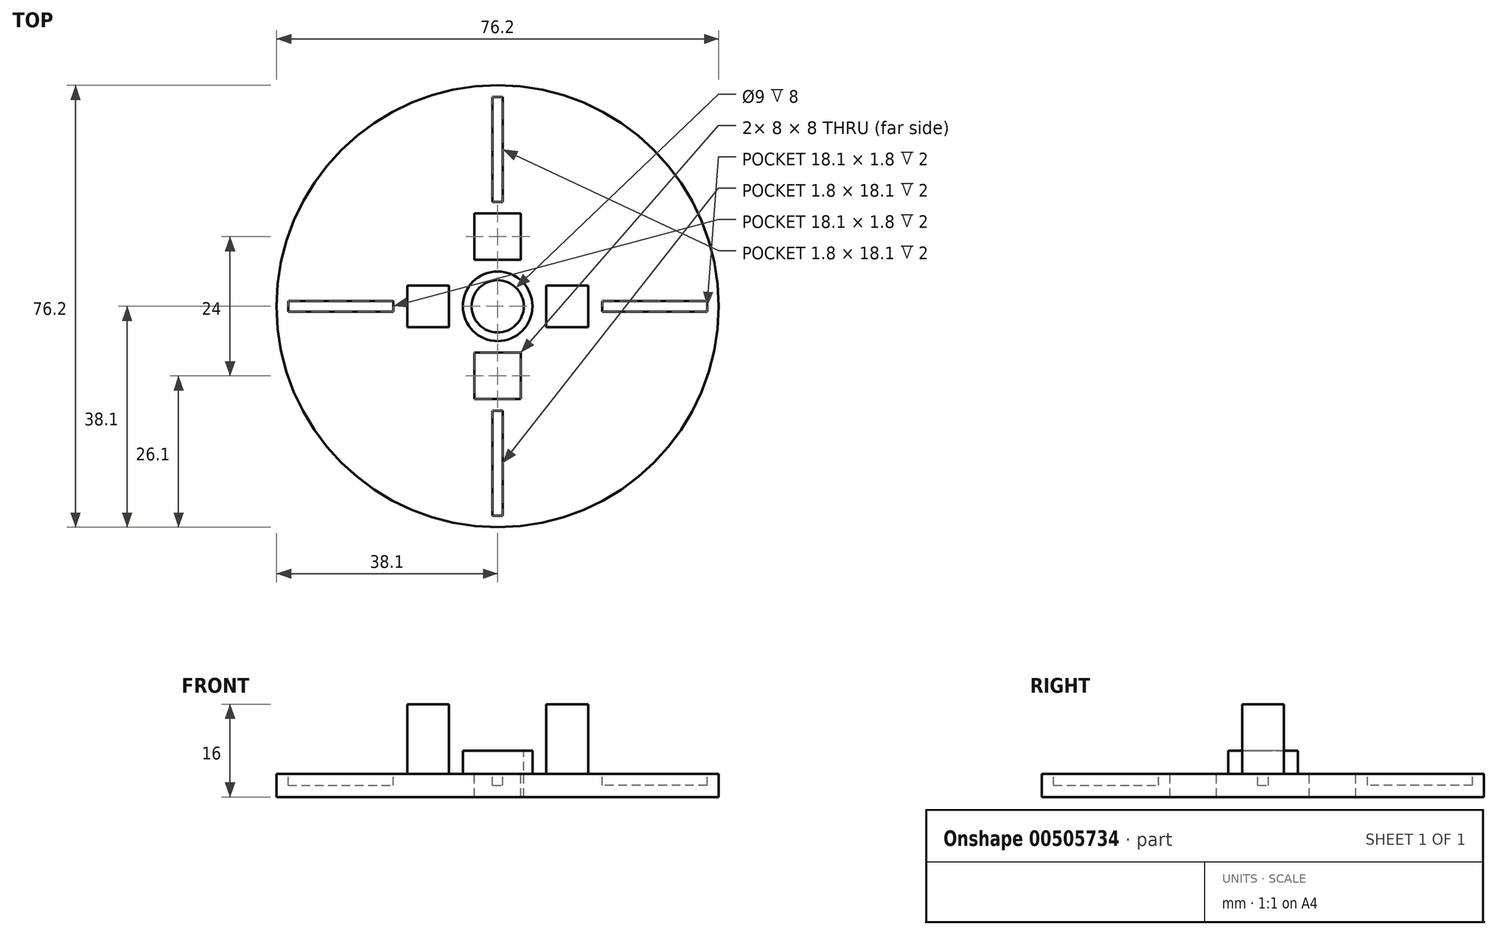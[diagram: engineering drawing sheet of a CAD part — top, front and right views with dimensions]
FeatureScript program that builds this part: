
annotation { "Feature Type Name" : "Feature", "Feature Type Description" : "" }
export const myFeature = defineFeature(function(context is Context, id is Id, definition is map)
    precondition{}
    {
        {
            var Q0;
            Q0=qCreatedBy(makeId("Top.planeOp"),FACE);
            var sketch = newSketch(context, id + "F0", { "sketchPlane" : qUnion([Q0])});
            skCircle(sketch, "E0", {"center": v(0, 0) * mm, "radius": 38.1 * mm});
            skSolve(sketch);
        }
        {
            var Q0;
            Q0 = qSketchRegion(id + "F0", true);
            extrude(context, id + "F1", {"entities" : qUnion([Q0]), "depth" : 4 * mm});
        }
        {
            var Q0;
            Q0=makeQuery(id+"F1.opExtrude","CAP_FACE",FACE,{"disambiguationData":[OSD([sQuery(id+"F0.wireOp",EDGE,"E0")])],"isStart":false});
            var sketch = newSketch(context, id + "F2", { "sketchPlane" : qUnion([Q0])});
            skLineSegment(sketch, "E1.bottom", {"start": v(4, 8) * mm, "end": v(-4, 8) * mm});
            skLineSegment(sketch, "E1.top", {"start": v(4, 16) * mm, "end": v(-4, 16) * mm});
            skLineSegment(sketch, "E1.left", {"start": v(4, 8) * mm, "end": v(4, 16) * mm});
            skLineSegment(sketch, "E1.right", {"start": v(-4, 8) * mm, "end": v(-4, 16) * mm});
            skPoint(sketch, "E1.middle", {"position": v(0, 12) * mm});
            skCircle(sketch, "E2", {"center": v(0, 0) * mm, "radius": 4.5 * mm});
            skCircle(sketch, "E3", {"center": v(0, 0) * mm, "radius": 6 * mm});
            skLineSegment(sketch, "E4.bottom", {"start": v(15.6, -3.6) * mm, "end": v(8.4, -3.6) * mm});
            skLineSegment(sketch, "E4.top", {"start": v(15.6, 3.6) * mm, "end": v(8.4, 3.6) * mm});
            skLineSegment(sketch, "E4.left", {"start": v(15.6, -3.6) * mm, "end": v(15.6, 3.6) * mm});
            skLineSegment(sketch, "E4.right", {"start": v(8.4, -3.6) * mm, "end": v(8.4, 3.6) * mm});
            skPoint(sketch, "E4.middle", {"position": v(12, 0) * mm});
            skLineSegment(sketch, "E5.MirrorCS", {"start": v(4, -8) * mm, "end": v(-4, -8) * mm});
            skLineSegment(sketch, "E6.MirrorCS", {"start": v(4, -8) * mm, "end": v(4, -16) * mm});
            skLineSegment(sketch, "E7.MirrorCS", {"start": v(4, -16) * mm, "end": v(-4, -16) * mm});
            skLineSegment(sketch, "E8.MirrorCS", {"start": v(-4, -8) * mm, "end": v(-4, -16) * mm});
            skLineSegment(sketch, "E9.MirrorCS", {"start": v(-8.4, -3.6) * mm, "end": v(-8.4, 3.6) * mm});
            skLineSegment(sketch, "E10.MirrorCS", {"start": v(-15.6, -3.6) * mm, "end": v(-8.4, -3.6) * mm});
            skLineSegment(sketch, "E11.MirrorCS", {"start": v(-15.6, -3.6) * mm, "end": v(-15.6, 3.6) * mm});
            skLineSegment(sketch, "E12.MirrorCS", {"start": v(-15.6, 3.6) * mm, "end": v(-8.4, 3.6) * mm});
            skSolve(sketch);
        }
        {
            var Q0;
            Q0=makeQuery(id+"F2.imprint","IMPRINT",FACE,{"disambiguationData":[TD([[makeQuery(id+"F2.imprint","IMPRINT",EDGE,{"derivedFrom":sQuery(id+"F2.wireOp",EDGE,"E2")}),1.0]])]});
            var Q1;
            Q1=makeQuery(id+"F2.imprint","IMPRINT",FACE,{"disambiguationData":[TD([[makeQuery(id+"F2.imprint","IMPRINT",EDGE,{"derivedFrom":sQuery(id+"F2.wireOp",EDGE,"E1.bottom")}),-1.0]])]});
            var Q2;
            Q2=makeQuery(id+"F2.imprint","IMPRINT",FACE,{"disambiguationData":[TD([[makeQuery(id+"F2.imprint","IMPRINT",EDGE,{"derivedFrom":sQuery(id+"F2.wireOp",EDGE,"E5.MirrorCS")}),1.0]])]});
            extrude(context, id + "F3", {"entities" : qUnion([Q0, Q1, Q2]), "operationType" : NewBodyOperationType.REMOVE, "endBound" : BoundingType.THROUGH_ALL, "oppositeDirection" : true, "depth" : 25 * mm});
        }
        {
            var Q0;
            Q0=makeQuery(id+"F2.imprint","IMPRINT",FACE,{"disambiguationData":[TD([[makeQuery(id+"F2.imprint","IMPRINT",EDGE,{"derivedFrom":sQuery(id+"F2.wireOp",EDGE,"E4.bottom")}),-1.0]])]});
            var Q1;
            Q1=makeQuery(id+"F2.imprint","IMPRINT",FACE,{"disambiguationData":[TD([[makeQuery(id+"F2.imprint","IMPRINT",EDGE,{"derivedFrom":sQuery(id+"F2.wireOp",EDGE,"E9.MirrorCS")}),1.0]])]});
            extrude(context, id + "F4", {"entities" : qUnion([Q0, Q1]), "operationType" : NewBodyOperationType.ADD, "depth" : 12 * mm});
        }
        {
            var Q0;
            Q0=makeQuery(id+"F2.imprint","IMPRINT",FACE,{"disambiguationData":[TD([[makeQuery(id+"F2.imprint","IMPRINT",EDGE,{"derivedFrom":sQuery(id+"F2.wireOp",EDGE,"E2")}),-1.0]])]});
            extrude(context, id + "F5", {"entities" : qUnion([Q0]), "operationType" : NewBodyOperationType.ADD, "depth" : 4 * mm});
        }
        {
            var Q0;
            Q0=makeQuery(id+"F1.opExtrude","CAP_FACE",FACE,{"disambiguationData":[OSD([sQuery(id+"F0.wireOp",EDGE,"E0")])],"isStart":false});
            var sketch = newSketch(context, id + "F6", { "sketchPlane" : qUnion([Q0])});
            skLineSegment(sketch, "E13.bottom", {"start": v(0.9, 36.1) * mm, "end": v(-0.9, 36.1) * mm});
            skLineSegment(sketch, "E13.top", {"start": v(0.9, 18) * mm, "end": v(-0.9, 18) * mm});
            skLineSegment(sketch, "E13.left", {"start": v(0.9, 36.1) * mm, "end": v(0.9, 18) * mm});
            skLineSegment(sketch, "E13.right", {"start": v(-0.9, 36.1) * mm, "end": v(-0.9, 18) * mm});
            skPoint(sketch, "E13.middle", {"position": v(0, 27.05) * mm});
            skLineSegment(sketch, "E14.1.0", {"start": v(-36.1, 0.9) * mm, "end": v(-18, 0.9) * mm});
            skLineSegment(sketch, "E14.1.1", {"start": v(-36.1, -0.9) * mm, "end": v(-18, -0.9) * mm});
            skLineSegment(sketch, "E14.1.2", {"start": v(-18, 0.9) * mm, "end": v(-18, -0.9) * mm});
            skLineSegment(sketch, "E14.1.3", {"start": v(-36.1, 0.9) * mm, "end": v(-36.1, -0.9) * mm});
            skLineSegment(sketch, "E14.2.0", {"start": v(-0.9, -36.1) * mm, "end": v(-0.9, -18) * mm});
            skLineSegment(sketch, "E14.2.1", {"start": v(0.9, -36.1) * mm, "end": v(0.9, -18) * mm});
            skLineSegment(sketch, "E14.2.2", {"start": v(-0.9, -18) * mm, "end": v(0.9, -18) * mm});
            skLineSegment(sketch, "E14.2.3", {"start": v(-0.9, -36.1) * mm, "end": v(0.9, -36.1) * mm});
            skLineSegment(sketch, "E14.3.0", {"start": v(36.1, -0.9) * mm, "end": v(18, -0.9) * mm});
            skLineSegment(sketch, "E14.3.1", {"start": v(36.1, 0.9) * mm, "end": v(18, 0.9) * mm});
            skLineSegment(sketch, "E14.3.2", {"start": v(18, -0.9) * mm, "end": v(18, 0.9) * mm});
            skLineSegment(sketch, "E14.3.3", {"start": v(36.1, -0.9) * mm, "end": v(36.1, 0.9) * mm});
            skPoint(sketch, "E14.center", {"position": v(0, 0) * mm});
            skSolve(sketch);
        }
        {
            var Q0;
            Q0 = qSketchRegion(id + "F6", true);
            extrude(context, id + "F7", {"entities" : qUnion([Q0]), "operationType" : NewBodyOperationType.REMOVE, "oppositeDirection" : true, "depth" : 2 * mm});
        }
    });
